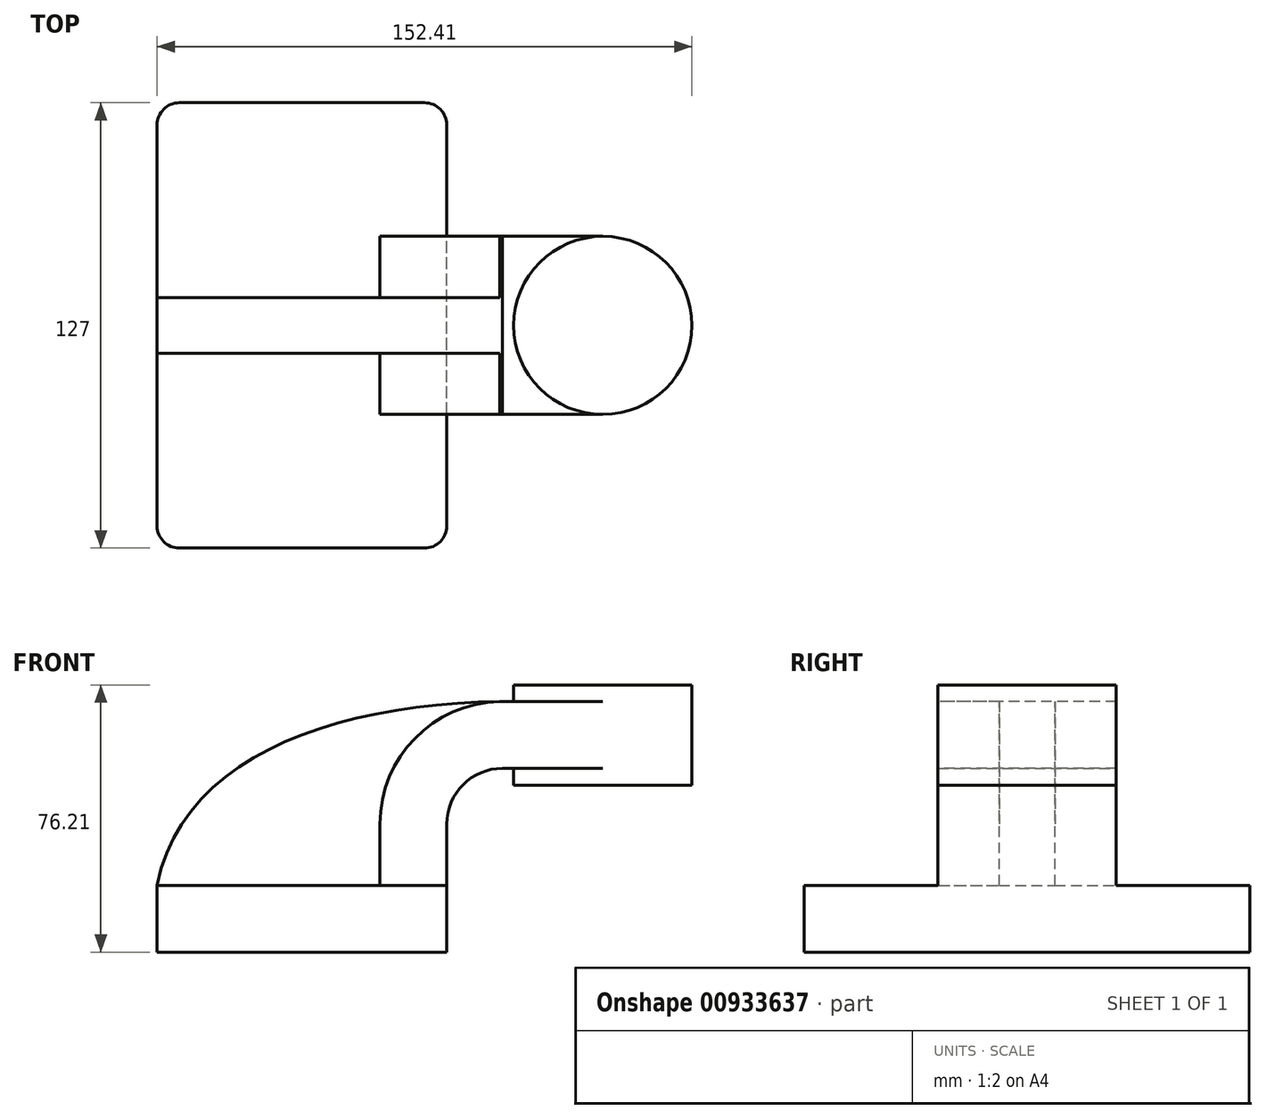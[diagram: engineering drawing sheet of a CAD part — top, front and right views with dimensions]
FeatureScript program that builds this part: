
annotation { "Feature Type Name" : "Feature", "Feature Type Description" : "" }
export const myFeature = defineFeature(function(context is Context, id is Id, definition is map)
    precondition{}
    {
        {
            var Q0;
            Q0=qCreatedBy(makeId("Front.planeOp"),FACE);
            var sketch = newSketch(context, id + "F0", { "sketchPlane" : qUnion([Q0])});
            skLineSegment(sketch, "E0.bottom", {"start": v(41.27, 9.53) * mm, "end": v(-41.28, 9.53) * mm});
            skLineSegment(sketch, "E0.top", {"start": v(41.28, -9.52) * mm, "end": v(-41.27, -9.52) * mm});
            skLineSegment(sketch, "E0.left", {"start": v(41.28, 9.53) * mm, "end": v(41.28, -9.52) * mm});
            skLineSegment(sketch, "E0.right", {"start": v(-41.28, 9.53) * mm, "end": v(-41.27, -9.52) * mm});
            skPoint(sketch, "E0.middle", {"position": v(0, 0) * mm});
            skLineSegment(sketch, "E1.bottom", {"start": v(60.32, 66.68) * mm, "end": v(111.12, 66.68) * mm});
            skLineSegment(sketch, "E1.top", {"start": v(60.32, 38.1) * mm, "end": v(111.12, 38.1) * mm});
            skLineSegment(sketch, "E1.left", {"start": v(60.32, 66.68) * mm, "end": v(60.32, 38.1) * mm});
            skLineSegment(sketch, "E1.right", {"start": v(111.12, 66.68) * mm, "end": v(111.12, 38.1) * mm});
            skPoint(sketch, "E1.middle", {"position": v(85.72, 52.39) * mm});
            skLineSegment(sketch, "E2", {"start": v(41.27, 9.53) * mm, "end": v(41.27, 27) * mm});
            skArc(sketch, "E3", {"start": v(41.27, 27) * mm, "mid": v(45.92, 38.23) * mm, "end": v(57.15, 42.88) * mm});
            skLineSegment(sketch, "E4", {"start": v(57.15, 42.88) * mm, "end": v(85.72, 42.88) * mm});
            skLineSegment(sketch, "E5.0", {"start": v(57.15, 61.93) * mm, "end": v(85.72, 61.93) * mm});
            skArc(sketch, "E5.1", {"start": v(22.22, 27) * mm, "mid": v(32.45, 51.7) * mm, "end": v(57.15, 61.93) * mm});
            skLineSegment(sketch, "E5.2", {"start": v(22.22, 9.53) * mm, "end": v(22.22, 27) * mm});
            skLineSegment(sketch, "E6", {"start": v(85.72, 66.68) * mm, "end": v(85.72, 38.1) * mm});
            skFitSpline(sketch, "E7", {"points": [v(-41.28, 9.52) * mm, v(57.15, 61.93) * mm], "startDerivative": vector(22.19, 111.88) * mm, "endDerivative": vector(140.3, 1.4) * mm});
            skSolve(sketch);
        }
        {
            var Q0;
            Q0=makeQuery(id+"F0.imprint","IMPRINT",FACE,{"disambiguationData":[TD([[makeQuery(id+"F0.imprint","IMPRINT",EDGE,{"derivedFrom":sQuery(id+"F0.wireOp",EDGE,"E0.top")}),-1.0]])]});
            extrude(context, id + "F1", {"entities" : qUnion([Q0]), "endBound" : BoundingType.SYMMETRIC, "depth" : 127 * mm, "offsetDistance" : 25.4 * mm});
        }
        {
            var Q0;
            {var subQ0=sQuery(id+"F0.wireOp",EDGE,"E5.0");var subQ1=sQuery(id+"F0.wireOp",EDGE,"E1.left");var subQ2=makeQuery(id+"F0.imprint","INTERSECT",VERTEX,{"derivedFrom":[subQ1,subQ0]});Q0=makeQuery(id+"F0.imprint","IMPRINT",FACE,{"disambiguationData":[TD([[makeQuery(id+"F0.imprint","IMPRINT",EDGE,{"disambiguationData":[TD([[subQ2,-1.0]])],"derivedFrom":subQ1}),1.0]])]});}
            var Q1;
            {var subQ1=sQuery(id+"F0.wireOp",EDGE,"E2");Q1=makeQuery(id+"F0.imprint","IMPRINT",FACE,{"disambiguationData":[TD([[makeQuery(id+"F0.imprint","IMPRINT",EDGE,{"derivedFrom":subQ1}),1.0]])]});}
            extrude(context, id + "F2", {"entities" : qUnion([Q0, Q1]), "operationType" : NewBodyOperationType.ADD, "endBound" : BoundingType.SYMMETRIC, "depth" : 50.8 * mm, "offsetDistance" : 25.4 * mm});
        }
        {
            var Q0;
            {var subQ3=sQuery(id+"F0.wireOp",EDGE,"E5.2");Q0=makeQuery(id+"F0.imprint","IMPRINT",FACE,{"disambiguationData":[TD([[makeQuery(id+"F0.imprint","IMPRINT",EDGE,{"derivedFrom":subQ3}),1.0]])]});}
            extrude(context, id + "F3", {"entities" : qUnion([Q0]), "operationType" : NewBodyOperationType.ADD, "endBound" : BoundingType.SYMMETRIC, "depth" : 15.88 * mm, "offsetDistance" : 25.4 * mm});
        }
        {
            var Q0;
            {var subQ4=sQuery(id+"F0.wireOp",EDGE,"E1.right");Q0=makeQuery(id+"F0.imprint","IMPRINT",FACE,{"disambiguationData":[TD([[makeQuery(id+"F0.imprint","IMPRINT",EDGE,{"derivedFrom":subQ4}),-1.0]])]});}
            var Q1;
            Q1=sQuery(id+"F0.wireOp",EDGE,"E6");
            revolve(context, id + "F4", {"operationType" : NewBodyOperationType.ADD, "surfaceOperationType" : NewSurfaceOperationType.NEW, "entities" : qUnion([Q0]), "axis" : qUnion([Q1]), "revolveType" : RevolveType.FULL});
        }
        {
            var Q0;
            Q0=makeQuery(id+"F1.opExtrude","CAP_EDGE",EDGE,{"disambiguationData":[OSD([sQuery(id+"F0.wireOp",EDGE,"E0.right")])],"isStart":false});
            var Q1;
            Q1=makeQuery(id+"F1.opExtrude","CAP_EDGE",EDGE,{"disambiguationData":[OSD([sQuery(id+"F0.wireOp",EDGE,"E0.right")])],"isStart":true});
            var Q2;
            Q2=makeQuery(id+"F1.opExtrude","CAP_EDGE",EDGE,{"disambiguationData":[OSD([sQuery(id+"F0.wireOp",EDGE,"E0.left")])],"isStart":true});
            var Q3;
            Q3=makeQuery(id+"F1.opExtrude","CAP_EDGE",EDGE,{"disambiguationData":[OSD([sQuery(id+"F0.wireOp",EDGE,"E0.left")])],"isStart":false});
            fillet(context, id + "F5", {"entities" : qUnion([Q0, Q1, Q2, Q3]), "radius" : 6.35 * mm, "tangentPropagation" : true, "allowEdgeOverflow" : false});
        }
    });
